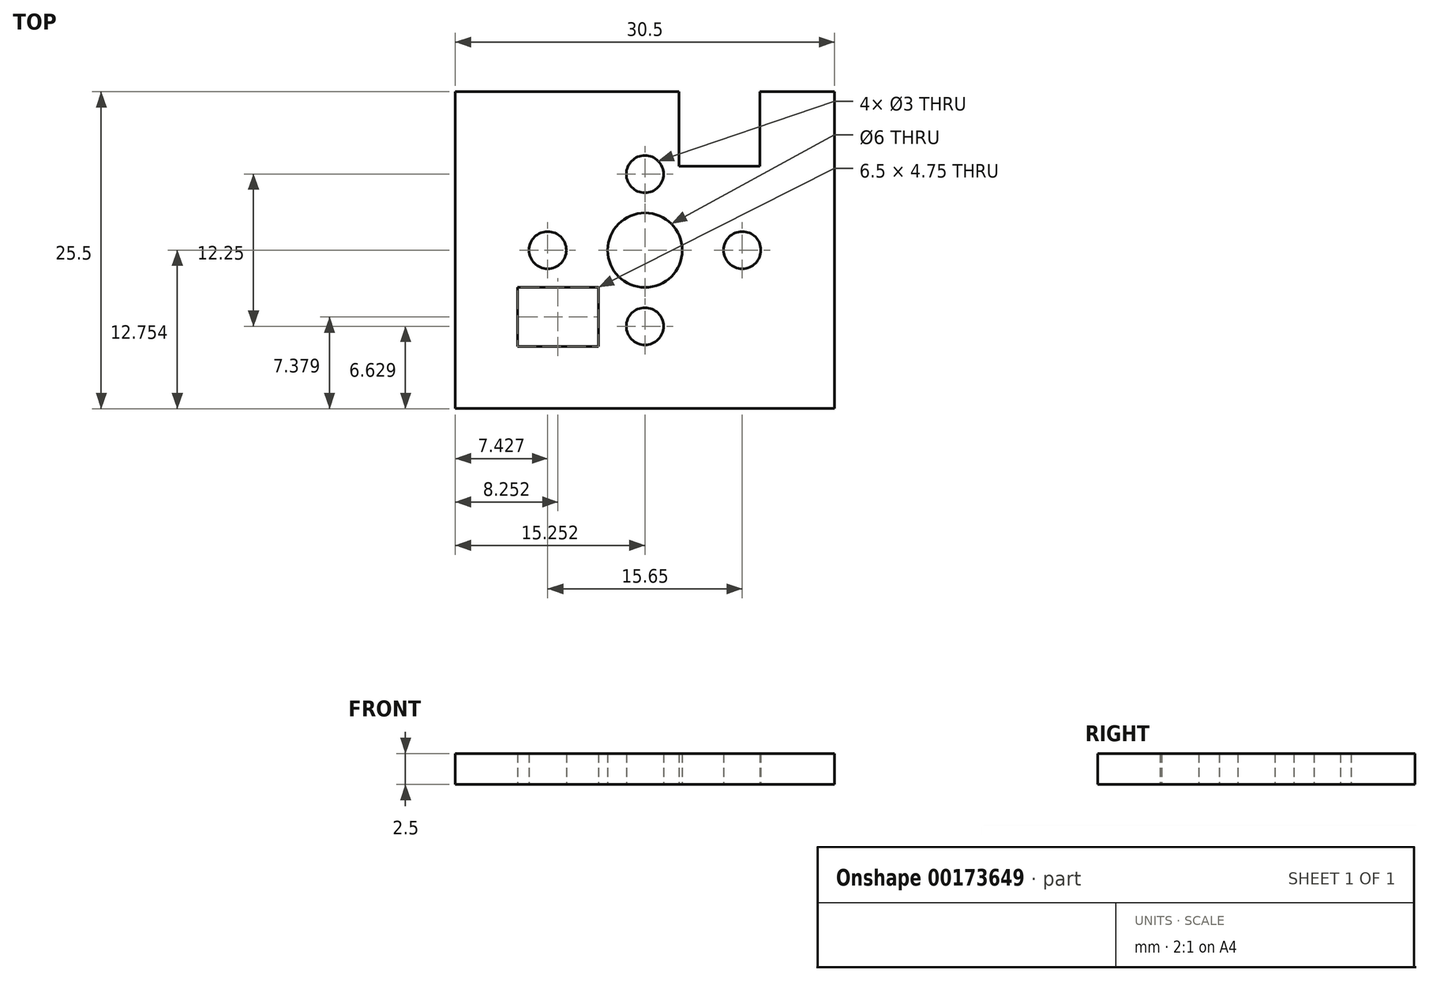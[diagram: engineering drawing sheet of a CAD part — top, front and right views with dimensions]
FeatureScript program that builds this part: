
annotation { "Feature Type Name" : "Feature", "Feature Type Description" : "" }
export const myFeature = defineFeature(function(context is Context, id is Id, definition is map)
    precondition{}
    {
        {
            var Q0;
            Q0=qCreatedBy(makeId("Top.planeOp"),FACE);
            var sketch = newSketch(context, id + "F0", { "sketchPlane" : qUnion([Q0])});
            skLineSegment(sketch, "E0.top", {"start": v(-39.99, 1.92) * mm, "end": v(-9.49, 1.92) * mm});
            skLineSegment(sketch, "E0.left", {"start": v(-39.99, 27.42) * mm, "end": v(-39.99, 1.92) * mm});
            skLineSegment(sketch, "E0.right", {"start": v(-9.49, 27.42) * mm, "end": v(-9.49, 1.92) * mm});
            skLineSegment(sketch, "E1", {"start": v(-24.74, 27.42) * mm, "end": v(-24.74, 1.92) * mm, "construction": true});
            skLineSegment(sketch, "E2", {"start": v(-39.99, 14.67) * mm, "end": v(-9.49, 14.67) * mm, "construction": true});
            skCircle(sketch, "E3", {"center": v(-24.74, 14.67) * mm, "radius": 3 * mm});
            skLineSegment(sketch, "E4.bottom", {"start": v(-39.99, 1.92) * mm, "end": v(-28.49, 1.92) * mm, "construction": true});
            skLineSegment(sketch, "E4.left", {"start": v(-39.99, 1.92) * mm, "end": v(-39.99, 10.92) * mm, "construction": true});
            skLineSegment(sketch, "E5.left", {"start": v(-9.49, 27.42) * mm, "end": v(-9.49, 23.67) * mm, "construction": true});
            skLineSegment(sketch, "E6", {"start": v(-39.99, 27.42) * mm, "end": v(-21.99, 27.42) * mm});
            skCircle(sketch, "E7", {"center": v(-24.74, 14.67) * mm, "radius": 7.83 * mm, "construction": true});
            skCircle(sketch, "E8", {"center": v(-32.56, 14.67) * mm, "radius": 1.5 * mm});
            skCircle(sketch, "E9", {"center": v(-16.91, 14.67) * mm, "radius": 1.5 * mm});
            skCircle(sketch, "E10", {"center": v(-24.74, 14.67) * mm, "radius": 6.12 * mm, "construction": true});
            skCircle(sketch, "E11", {"center": v(-24.74, 20.8) * mm, "radius": 1.5 * mm});
            skCircle(sketch, "E12", {"center": v(-24.74, 8.55) * mm, "radius": 1.5 * mm});
            skLineSegment(sketch, "E13", {"start": v(-9.49, 27.42) * mm, "end": v(-15.49, 27.42) * mm});
            skCircle(sketch, "E14", {"center": v(-18.61, 14.67) * mm, "radius": 1.5 * mm, "construction": true});
            skCircle(sketch, "E15", {"center": v(-30.86, 14.67) * mm, "radius": 1.5 * mm, "construction": true});
            skCircle(sketch, "E16", {"center": v(-39.99, 1.92) * mm, "radius": 5 * mm, "construction": true});
            skLineSegment(sketch, "E17", {"start": v(-39.99, 6.92) * mm, "end": v(-5.92, 6.92) * mm, "construction": true});
            skLineSegment(sketch, "E18", {"start": v(-28.49, 1.92) * mm, "end": v(-28.49, 36.8) * mm, "construction": true});
            skLineSegment(sketch, "E19.bottom", {"start": v(-28.49, 6.92) * mm, "end": v(-34.99, 6.92) * mm});
            skLineSegment(sketch, "E19.top", {"start": v(-28.49, 11.67) * mm, "end": v(-34.99, 11.67) * mm});
            skLineSegment(sketch, "E19.left", {"start": v(-28.49, 6.92) * mm, "end": v(-28.49, 11.67) * mm});
            skLineSegment(sketch, "E19.right", {"start": v(-34.99, 6.92) * mm, "end": v(-34.99, 11.67) * mm});
            skLineSegment(sketch, "E20", {"start": v(-15.49, 27.42) * mm, "end": v(-15.49, 21.42) * mm});
            skLineSegment(sketch, "E21", {"start": v(-15.49, 21.42) * mm, "end": v(-21.99, 21.42) * mm});
            skLineSegment(sketch, "E22", {"start": v(-21.99, 21.42) * mm, "end": v(-21.99, 27.42) * mm});
            skSolve(sketch);
        }
        {
            var Q0;
            Q0=makeQuery(id+"F0.imprint","IMPRINT",FACE,{"disambiguationData":[TD([[makeQuery(id+"F0.imprint","IMPRINT",EDGE,{"derivedFrom":sQuery(id+"F0.wireOp",EDGE,"E0.top")}),1.0]])]});
            extrude(context, id + "F1", {"entities" : qUnion([Q0]), "depth" : 2.5 * mm});
        }
    });
